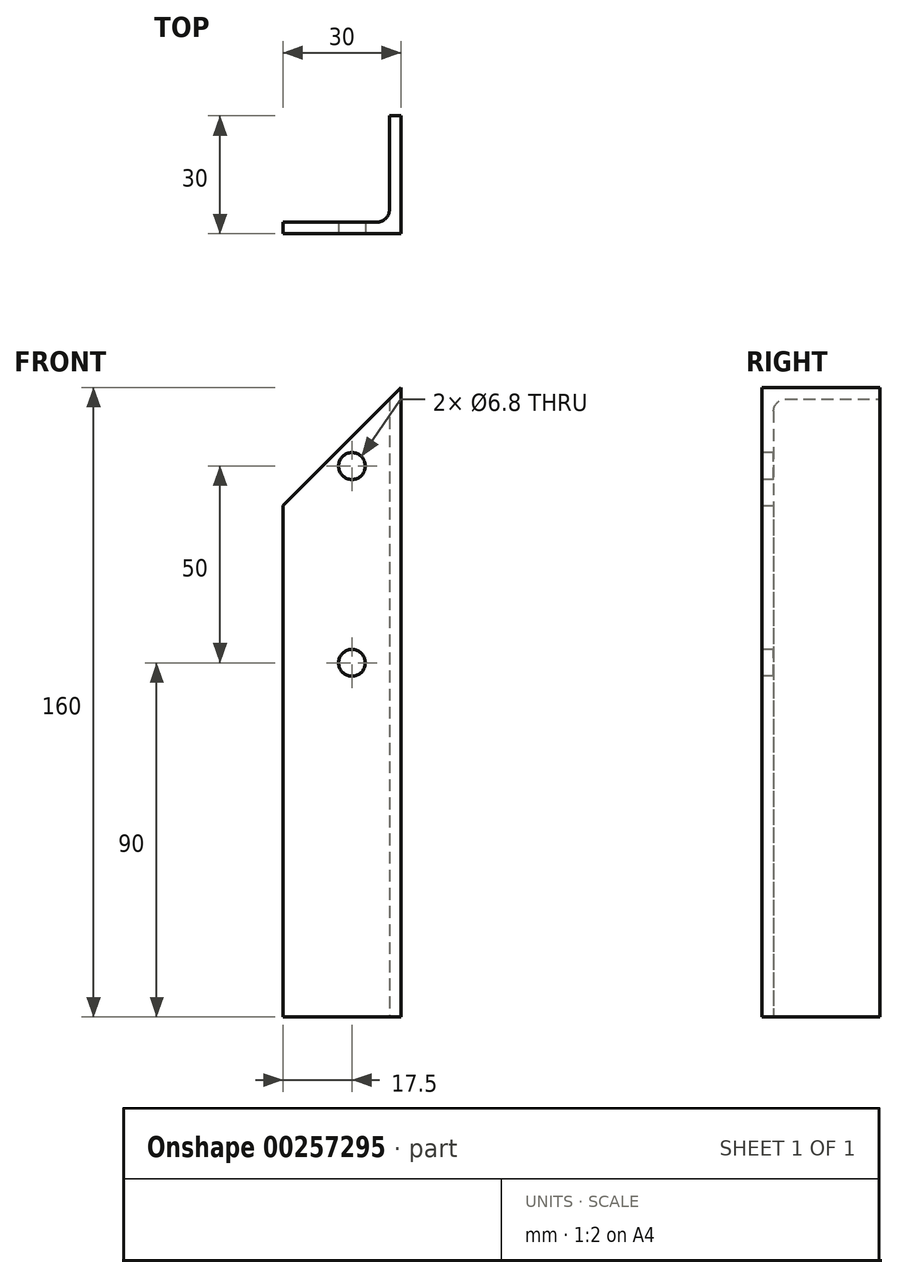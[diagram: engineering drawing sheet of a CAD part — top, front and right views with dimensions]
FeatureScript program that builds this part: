
annotation { "Feature Type Name" : "Feature", "Feature Type Description" : "" }
export const myFeature = defineFeature(function(context is Context, id is Id, definition is map)
    precondition{}
    {
        {
            var Q0;
            Q0=qCreatedBy(makeId("Top.planeOp"),FACE);
            var sketch = newSketch(context, id + "F0", { "sketchPlane" : qUnion([Q0])});
            skLineSegment(sketch, "E0", {"start": v(0, 0) * mm, "end": v(0, 3) * mm});
            skLineSegment(sketch, "E1", {"start": v(0, 0) * mm, "end": v(30, 0) * mm});
            skLineSegment(sketch, "E2", {"start": v(30, 0) * mm, "end": v(30, 30) * mm});
            skLineSegment(sketch, "E3", {"start": v(27, 30) * mm, "end": v(30, 30) * mm});
            skLineSegment(sketch, "E4", {"start": v(27, 3) * mm, "end": v(27, 30) * mm});
            skLineSegment(sketch, "E5", {"start": v(27, 3) * mm, "end": v(0, 3) * mm});
            skSolve(sketch);
        }
        {
            var Q0;
            Q0=makeQuery(id+"F0.imprint","IMPRINT",FACE,{"disambiguationData":[TD([[makeQuery(id+"F0.imprint","IMPRINT",EDGE,{"derivedFrom":sQuery(id+"F0.wireOp",EDGE,"E0")}),-1.0]])]});
            extrude(context, id + "F1", {"entities" : qUnion([Q0]), "depth" : 160 * mm});
        }
        {
            var Q0;
            Q0=makeQuery(id+"F1.opExtrude","SWEPT_EDGE",EDGE,{"disambiguationData":[OSD([sQuery(id+"F0.wireOp",EDGE,"E4"),sQuery(id+"F0.wireOp",EDGE,"E5")])]});
            fillet(context, id + "F2", {"entities" : qUnion([Q0]), "radius" : 3 * mm, "tangentPropagation" : true, "allowEdgeOverflow" : false});
        }
        {
            var Q0;
            Q0=makeQuery(id+"F1.opExtrude","SWEPT_FACE",FACE,{"disambiguationData":[OSD([sQuery(id+"F0.wireOp",EDGE,"E1")])]});
            var sketch = newSketch(context, id + "F3", { "sketchPlane" : qUnion([Q0])});
            skLineSegment(sketch, "E6", {"start": v(40, 170) * mm, "end": v(-10, 120) * mm});
            skLineSegment(sketch, "E7", {"start": v(-10, 120) * mm, "end": v(-10, 170) * mm});
            skLineSegment(sketch, "E8", {"start": v(40, 170) * mm, "end": v(-10, 170) * mm});
            skPoint(sketch, "E9", {"position": v(30, 160) * mm});
            skPoint(sketch, "E10", {"position": v(0, 130) * mm});
            skSolve(sketch);
        }
        {
            var Q0;
            Q0=qSketchRegion(id+"F3",true);
            extrude(context, id + "F4", {"entities" : qUnion([Q0]), "operationType" : NewBodyOperationType.REMOVE, "endBound" : BoundingType.THROUGH_ALL, "oppositeDirection" : true, "depth" : 25 * mm});
        }
        {
            var Q0;
            Q0=makeQuery(id+"F1.opExtrude","SWEPT_FACE",FACE,{"disambiguationData":[OSD([sQuery(id+"F0.wireOp",EDGE,"E1")])]});
            var sketch = newSketch(context, id + "F5", { "sketchPlane" : qUnion([Q0])});
            skPoint(sketch, "E11", {"position": v(17.5, 140) * mm});
            skPoint(sketch, "E12", {"position": v(17.5, 90) * mm});
            skSolve(sketch);
        }
        {
            var Q0;
            Q0=sQuery(id+"F5.wireOp",VERTEX,"E11");
            var Q1;
            Q1=sQuery(id+"F5.wireOp",VERTEX,"E12");
            var Q2;
            Q2=makeQuery(id+"F1.opExtrude","SWEPT_BODY",BODY,{"disambiguationData":[OSD([sQuery(id+"F0.wireOp",EDGE,"E0"),sQuery(id+"F0.wireOp",EDGE,"E1"),sQuery(id+"F0.wireOp",EDGE,"E2"),sQuery(id+"F0.wireOp",EDGE,"E3"),sQuery(id+"F0.wireOp",EDGE,"E4"),sQuery(id+"F0.wireOp",EDGE,"E5")])]});
            hole(context, id + "F6", {"style" : HoleStyle.SIMPLE, "endStyle" : HoleEndStyle.THROUGH, "standardTappedOrClearance" : lookupTablePath({ "standard" : "ISO", "fit" : "Normal", "engagement" : "75%", "pitch" : "1.25 mm", "size" : "M8", "type" : "Tapped" }), "standardBlindInLast" : lookupTablePath({ "fit" : "Standard", "standard" : "ISO", "engagement" : "75%", "pitch" : "1.25 mm", "size" : "M8", "type" : "Tapped" }), "holeDiameter" : 6.8 * mm, "showTappedDepth" : true, "tappedDepth" : 12 * mm, "tapClearance" : 3, "locations" : qUnion([Q0, Q1]), "scope" : qUnion([Q2]), "majorDiameter" : 8 * mm});
        }
    });
